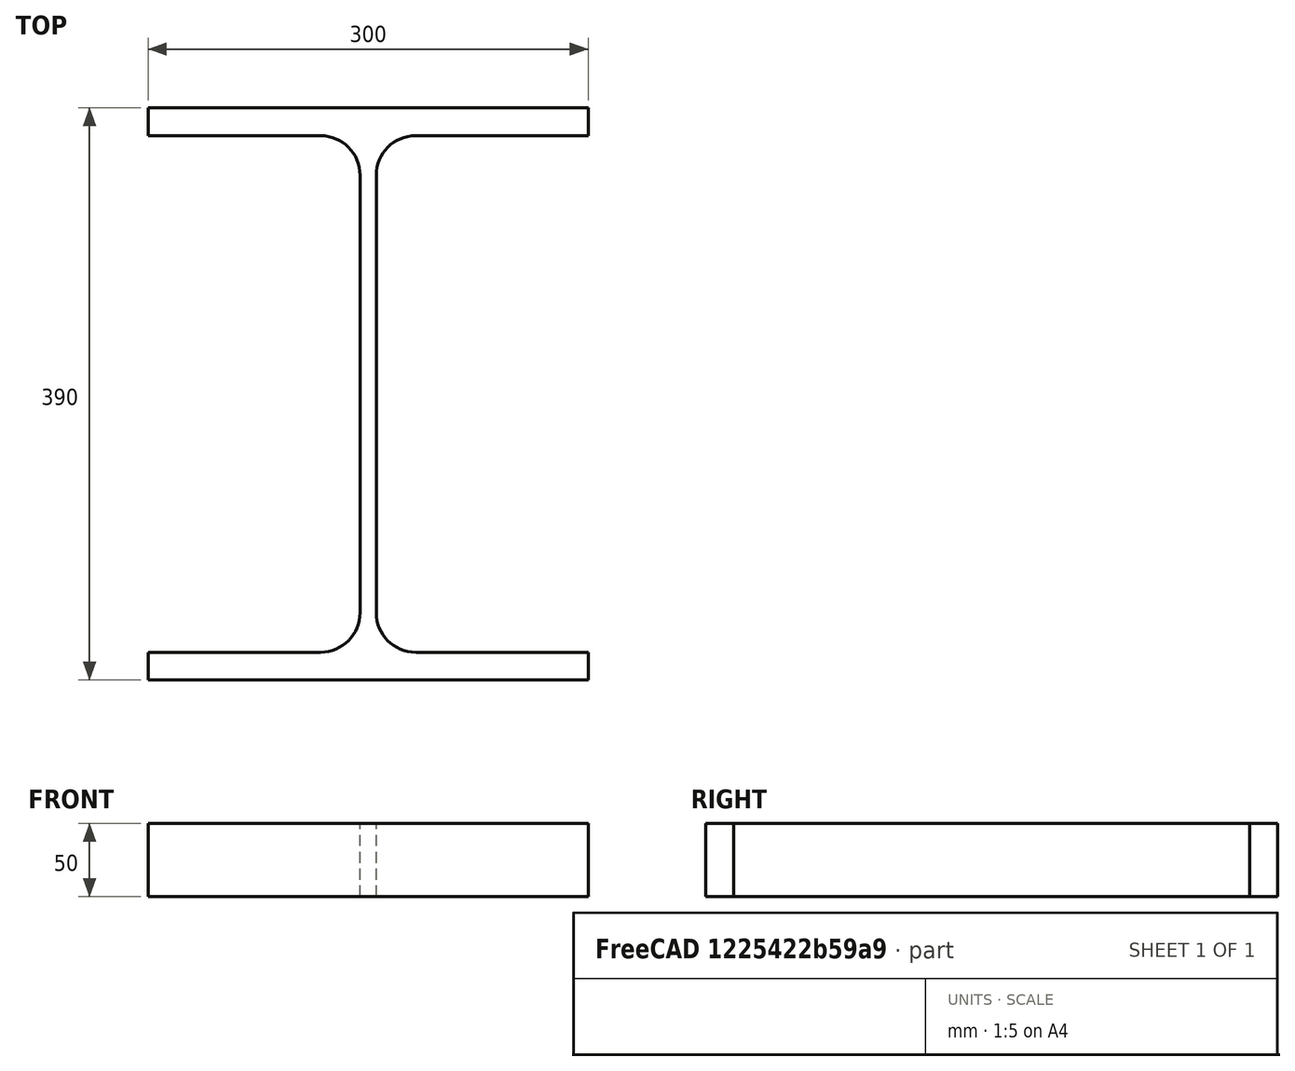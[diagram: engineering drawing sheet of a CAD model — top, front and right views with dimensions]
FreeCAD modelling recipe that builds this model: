
FCSTD DOCUMENT  (FreeCAD 0.15R4671 (Git))
Label: HE-A-Profile 400 DIN1025-3 S235JR
License: All rights reserved
LicenseURL: http://en.wikipedia.org/wiki/All_rights_reserved
objects: Sketcher::SketchObject×1, Part::Extrusion×1
note: 2 computed .brp shape members not serialized (recipe doc carries the construction recipe); baked Part::Feature solids carry a one-line shape summary decoded from their .brp

FEATURE [Sketcher::SketchObject] Sketch
  sketch-geometry (16):
    g0: LineSegment StartX=5.5 StartY=-149 StartZ=0 EndX=5.5 EndY=149 EndZ=0
    g1: LineSegment StartX=32.5 StartY=176 StartZ=0 EndX=150 EndY=176 EndZ=0
    g2: LineSegment StartX=150 StartY=176 StartZ=0 EndX=150 EndY=195 EndZ=0
    g3: LineSegment StartX=150 StartY=195 StartZ=0 EndX=-150 EndY=195 EndZ=0
    g4: LineSegment StartX=-150 StartY=195 StartZ=0 EndX=-150 EndY=176 EndZ=0
    g5: LineSegment StartX=-150 StartY=176 StartZ=0 EndX=-32.5 EndY=176 EndZ=0
    g6: LineSegment StartX=-5.5 StartY=149 StartZ=0 EndX=-5.5 EndY=-149 EndZ=0
    g7: LineSegment StartX=-32.5 StartY=-176 StartZ=0 EndX=-150 EndY=-176 EndZ=0
    g8: LineSegment StartX=-150 StartY=-176 StartZ=0 EndX=-150 EndY=-195 EndZ=0
    g9: LineSegment StartX=-150 StartY=-195 StartZ=0 EndX=150 EndY=-195 EndZ=0
    g10: LineSegment StartX=150 StartY=-195 StartZ=0 EndX=150 EndY=-176 EndZ=0
    g11: LineSegment StartX=150 StartY=-176 StartZ=0 EndX=32.5 EndY=-176 EndZ=0
    g12: ArcOfCircle CenterX=32.5 CenterY=149 CenterZ=0 NormalX=0 NormalY=0 NormalZ=1 Radius=27 StartAngle=1.5708 EndAngle=3.14159
    g13: ArcOfCircle CenterX=32.5 CenterY=-149 CenterZ=0 NormalX=0 NormalY=0 NormalZ=1 Radius=27 StartAngle=3.14159 EndAngle=4.71239
    g14: ArcOfCircle CenterX=-32.5 CenterY=149 CenterZ=0 NormalX=0 NormalY=0 NormalZ=1 Radius=27 StartAngle=0 EndAngle=1.5708
    g15: ArcOfCircle CenterX=-32.5 CenterY=-149 CenterZ=0 NormalX=0 NormalY=0 NormalZ=1 Radius=27 StartAngle=4.71239 EndAngle=6.28319
  constraints (42):
    c: Vertical(g0)
    c: Coincident(g2,g1)
    c: Vertical(g2)
    c: Coincident(g3,g2)
    c: Coincident(g4,g3)
    c: Vertical(g4)
    c: Coincident(g5,g4)
    c: Horizontal(g5)
    c: Vertical(g6)
    c: Horizontal(g7)
    c: Coincident(g8,g7)
    c: Vertical(g8)
    c: Coincident(g9,g8)
    c: Horizontal(g9)
    c: Coincident(g10,g9)
    c: Vertical(g10)
    c: Coincident(g11,g10)
    c: Horizontal(g11)
    c: Tangent(g1,g12) = 1.5708
    c: Tangent(g0,g12) = 1.5708
    c: Tangent(g0,g13) = 1.5708
    c: Tangent(g11,g13) = 1.5708
    c: Tangent(g5,g14) = 1.5708
    c: Tangent(g6,g14) = 1.5708
    c: Tangent(g6,g15) = 1.5708
    c: Tangent(g7,g15) = 1.5708
    c: Equal(g3,g9)
    c: Equal(g2,g4)
    c: Equal(g4,g8)
    c: Equal(g8,g10)
    c: Equal(g12,g14)
    c: Equal(g14,g15)
    c: Equal(g15,g13)
    c: Symmetric(g2,g3,g-2)
    c: Symmetric(g9,g8,g-2)
    c: Symmetric(g0,g6,g-2)
    c: Symmetric(g2,g9,g-1)
    c: DistanceY(g2,g9) = -390
    c: DistanceX(g3) = -300
    c: DistanceX(g0,g6) = -11
    c: DistanceY(g2) = 19
    c: Radius(g12) = 27
FEATURE [Part::Extrusion] Extrude  label="HE-A-Profile 400 DIN1025-3 S235JR"
  Base = -> Sketch
  Dir = (0,0,50)
  Solid = true
